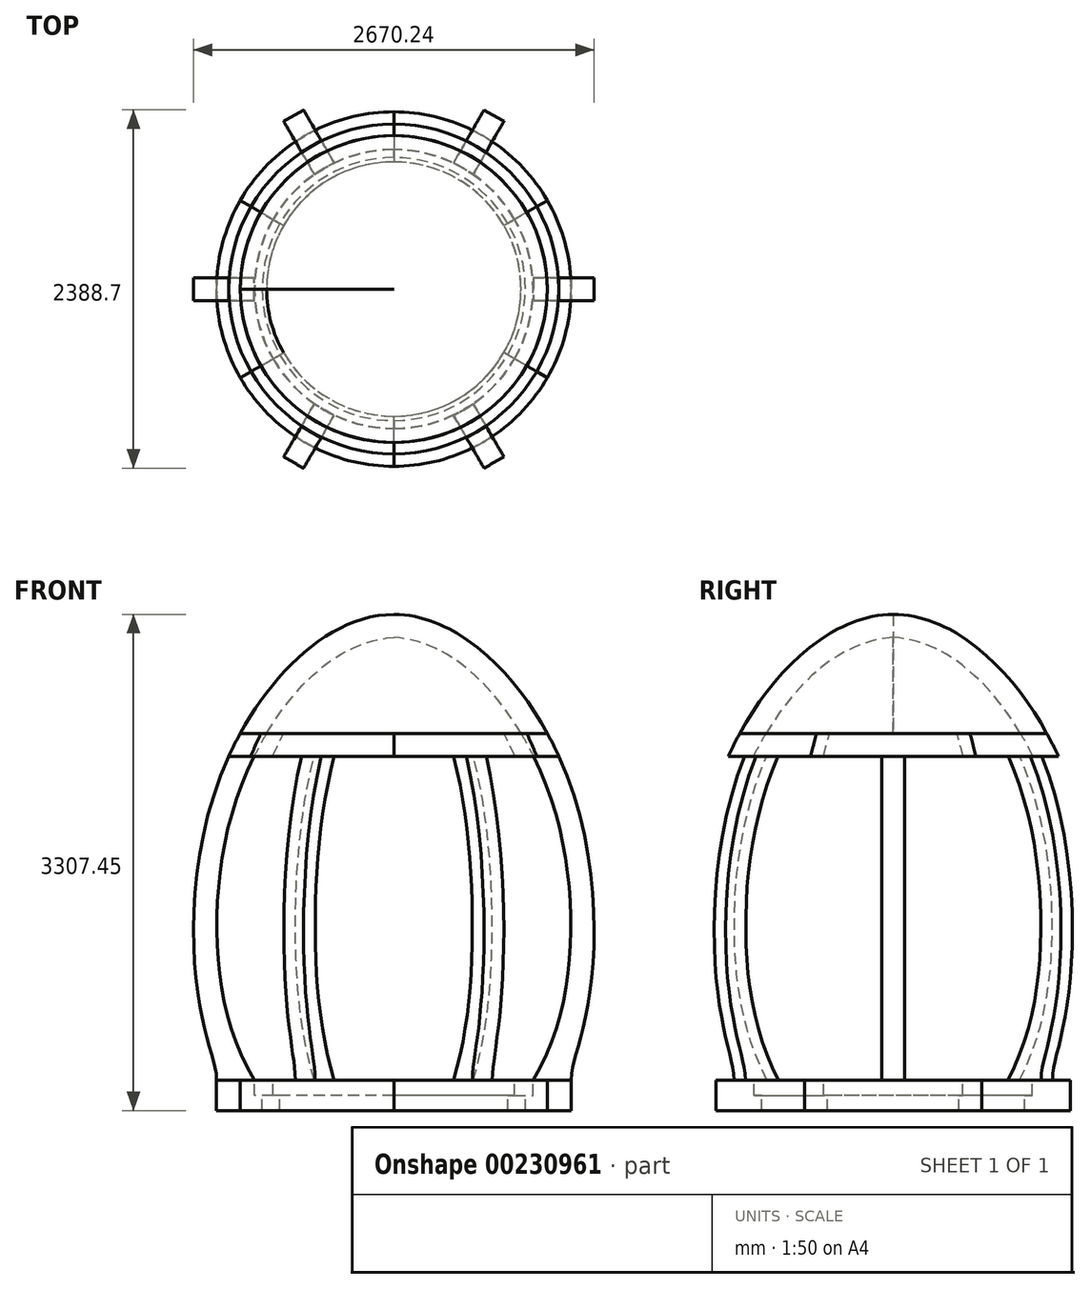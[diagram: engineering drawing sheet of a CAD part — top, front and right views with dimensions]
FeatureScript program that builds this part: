
annotation { "Feature Type Name" : "Feature", "Feature Type Description" : "" }
export const myFeature = defineFeature(function(context is Context, id is Id, definition is map)
    precondition{}
    {
        {
            var Q0;
            Q0=qCreatedBy(makeId("Front.planeOp"),FACE);
            var sketch = newSketch(context, id + "F0", { "sketchPlane" : qUnion([Q0])});
            skLineSegment(sketch, "E0", {"start": v(-1181.84, -1150.9) * mm, "end": v(-927.84, -1150.9) * mm});
            skFitSpline(sketch, "E1", {"points": [v(0, 1953.34) * mm, v(-1100.72, 1005.82) * mm, v(-1321.31, -446.03) * mm, v(-1216.83, -971.67) * mm, v(-1181.84, -1150.9) * mm], "startDerivative": vector(-4000.43, 5.06) * mm, "endDerivative": vector(0, -1489.55) * mm});
            skLineSegment(sketch, "E2", {"start": v(-1099.69, 1008.1) * mm, "end": v(-930.94, 1008.1) * mm});
            skLineSegment(sketch, "E3", {"start": v(-1181.84, -1150.9) * mm, "end": v(-1181.84, -1354.1) * mm});
            skLineSegment(sketch, "E4", {"start": v(-1181.84, -1354.1) * mm, "end": v(-877.04, -1354.1) * mm});
            skLineSegment(sketch, "E5", {"start": v(-877.04, -1354.1) * mm, "end": v(-877.04, -1252.5) * mm});
            skLineSegment(sketch, "E6", {"start": v(-877.04, -1252.5) * mm, "end": v(-927.84, -1252.5) * mm});
            skLineSegment(sketch, "E7", {"start": v(-927.84, -1252.5) * mm, "end": v(-927.84, -1150.9) * mm});
            skFitSpline(sketch, "E8.trimOffspring", {"points": [v(0, -1757.92) * mm, v(-927.84, -1150.9) * mm, v(-1179.31, -127.8) * mm, v(-917.89, 1034.08) * mm, v(0, 1800.66) * mm], "startDerivative": vector(-4973.2, 113.59) * mm, "endDerivative": vector(4756.7, 336.76) * mm});
            skLineSegment(sketch, "E9", {"start": v(-1023.33, 1160.5) * mm, "end": v(-848.12, 1160.5) * mm});
            skLineSegment(sketch, "E10", {"start": v(0, 1953.34) * mm, "end": v(0, 1800.66) * mm});
            skSolve(sketch);
        }
        {
            var Q0;
            {var subQ0=sQuery(id+"F0.wireOp",EDGE,"E0");Q0=makeQuery(id+"F0.imprint","IMPRINT",FACE,{"disambiguationData":[TD([[makeQuery(id+"F0.imprint","IMPRINT",EDGE,{"derivedFrom":subQ0}),1.0]])]});}
            extrude(context, id + "F1", {"entities" : qUnion([Q0]), "endBound" : BoundingType.SYMMETRIC, "depth" : 152.4 * mm});
        }
        {
            var Q0;
            Q0=makeQuery(id+"F1.opExtrude","SWEPT_BODY",BODY,{"disambiguationData":[OSD([sQuery(id+"F0.wireOp",EDGE,"E0"),sQuery(id+"F0.wireOp",EDGE,"E1"),sQuery(id+"F0.wireOp",EDGE,"E2"),sQuery(id+"F0.wireOp",EDGE,"E8.trimOffspring")])]});
            var Q1;
            Q1=sQuery(id+"F0.wireOp",EDGE,"E10");
            circularPattern(context, id + "F2", {"entities" : qUnion([Q0]), "axis" : qUnion([Q1]), "angle" : 360 * degree, "instanceCount" : 6, "equalSpace" : true});
        }
        {
            var Q0;
            {var subQ0=sQuery(id+"F0.wireOp",EDGE,"E2");Q0=makeQuery(id+"F0.imprint","IMPRINT",FACE,{"disambiguationData":[TD([[makeQuery(id+"F0.imprint","IMPRINT",EDGE,{"derivedFrom":subQ0}),1.0]])]});}
            var Q1;
            Q1=sQuery(id+"F0.wireOp",EDGE,"E10");
            revolve(context, id + "F3", {"entities" : qUnion([Q0]), "axis" : qUnion([Q1]), "revolveType" : RevolveType.SYMMETRIC, "angle" : 60 * degree});
        }
        {
            var Q0;
            Q0=makeQuery(id+"F3.opRevolve","SWEPT_BODY",BODY,{"disambiguationData":[OSD([sQuery(id+"F0.wireOp",EDGE,"E1"),sQuery(id+"F0.wireOp",EDGE,"E2"),sQuery(id+"F0.wireOp",EDGE,"E8.trimOffspring"),sQuery(id+"F0.wireOp",EDGE,"E9")])]});
            var Q1;
            Q1=sQuery(id+"F0.wireOp",EDGE,"E10");
            circularPattern(context, id + "F4", {"entities" : qUnion([Q0]), "axis" : qUnion([Q1]), "angle" : 360 * degree, "instanceCount" : 6, "equalSpace" : true});
        }
        {
            var Q0;
            Q0=makeQuery(id+"F0.imprint","IMPRINT",FACE,{"disambiguationData":[TD([[makeQuery(id+"F0.imprint","IMPRINT",EDGE,{"derivedFrom":sQuery(id+"F0.wireOp",EDGE,"E0")}),-1.0]])]});
            var Q1;
            Q1=sQuery(id+"F0.wireOp",EDGE,"E10");
            revolve(context, id + "F5", {"entities" : qUnion([Q0]), "axis" : qUnion([Q1]), "revolveType" : RevolveType.SYMMETRIC, "angle" : 60 * degree});
        }
        {
            var Q0;
            Q0=makeQuery(id+"F5.opRevolve","SWEPT_BODY",BODY,{"disambiguationData":[OSD([sQuery(id+"F0.wireOp",EDGE,"E0"),sQuery(id+"F0.wireOp",EDGE,"E3"),sQuery(id+"F0.wireOp",EDGE,"E4"),sQuery(id+"F0.wireOp",EDGE,"E5"),sQuery(id+"F0.wireOp",EDGE,"E6"),sQuery(id+"F0.wireOp",EDGE,"E7")])]});
            var Q1;
            Q1=sQuery(id+"F0.wireOp",EDGE,"E10");
            circularPattern(context, id + "F6", {"entities" : qUnion([Q0]), "axis" : qUnion([Q1]), "angle" : 360 * degree, "instanceCount" : 6, "equalSpace" : true});
        }
        {
            var Q0;
            {var subQ2=sQuery(id+"F0.wireOp",EDGE,"E9");Q0=makeQuery(id+"F0.imprint","IMPRINT",FACE,{"disambiguationData":[TD([[makeQuery(id+"F0.imprint","IMPRINT",EDGE,{"derivedFrom":subQ2}),1.0]])]});}
            var Q1;
            Q1=sQuery(id+"F0.wireOp",EDGE,"E10");
            revolve(context, id + "F7", {"entities" : qUnion([Q0]), "axis" : qUnion([Q1]), "revolveType" : RevolveType.FULL});
        }
    });
